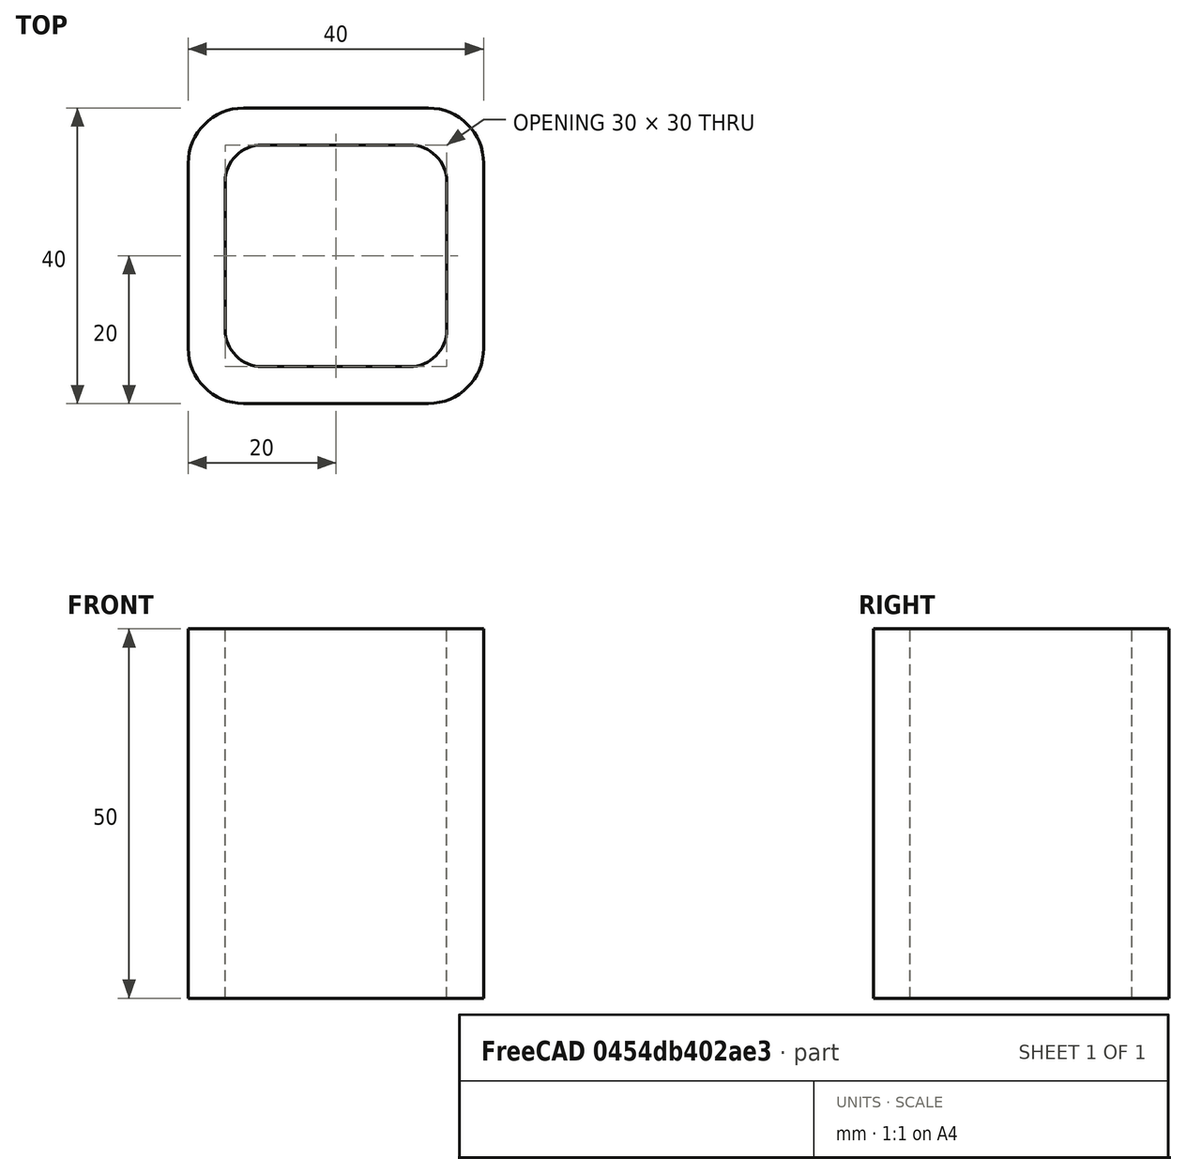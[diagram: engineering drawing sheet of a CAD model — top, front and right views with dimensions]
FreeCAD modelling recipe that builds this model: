
FCSTD DOCUMENT  (FreeCAD 0.15R4671 (Git))
Label: Square hollow section 40x40x5 EN10219 S235JRH
License: All rights reserved
LicenseURL: http://en.wikipedia.org/wiki/All_rights_reserved
objects: Sketcher::SketchObject×1, Part::Extrusion×1
note: 2 computed .brp shape members not serialized (recipe doc carries the construction recipe); baked Part::Feature solids carry a one-line shape summary decoded from their .brp

FEATURE [Sketcher::SketchObject] Sketch
  sketch-geometry (16):
    g0: LineSegment StartX=-10 StartY=15 StartZ=0 EndX=10 EndY=15 EndZ=0
    g1: LineSegment StartX=15 StartY=10 StartZ=0 EndX=15 EndY=-10 EndZ=0
    g2: LineSegment StartX=10 StartY=-15 StartZ=0 EndX=-10 EndY=-15 EndZ=0
    g3: LineSegment StartX=-15 StartY=-10 StartZ=0 EndX=-15 EndY=10 EndZ=0
    g4: LineSegment StartX=-12.5 StartY=20 StartZ=0 EndX=12.5 EndY=20 EndZ=0
    g5: LineSegment StartX=20 StartY=12.5 StartZ=0 EndX=20 EndY=-12.5 EndZ=0
    g6: LineSegment StartX=12.5 StartY=-20 StartZ=0 EndX=-12.5 EndY=-20 EndZ=0
    g7: LineSegment StartX=-20 StartY=-12.5 StartZ=0 EndX=-20 EndY=12.5 EndZ=0
    g8: ArcOfCircle CenterX=-10 CenterY=10 CenterZ=0 NormalX=0 NormalY=0 NormalZ=1 Radius=5 StartAngle=1.5708 EndAngle=3.14159
    g9: ArcOfCircle CenterX=10 CenterY=10 CenterZ=0 NormalX=0 NormalY=0 NormalZ=1 Radius=5 StartAngle=0 EndAngle=1.5708
    g10: ArcOfCircle CenterX=10 CenterY=-10 CenterZ=0 NormalX=0 NormalY=0 NormalZ=1 Radius=5 StartAngle=4.71239 EndAngle=6.28319
    g11: ArcOfCircle CenterX=-10 CenterY=-10 CenterZ=0 NormalX=0 NormalY=0 NormalZ=1 Radius=5 StartAngle=3.14159 EndAngle=4.71239
    g12: ArcOfCircle CenterX=12.5 CenterY=12.5 CenterZ=0 NormalX=0 NormalY=0 NormalZ=1 Radius=7.5 StartAngle=0 EndAngle=1.5708
    g13: ArcOfCircle CenterX=12.5 CenterY=-12.5 CenterZ=0 NormalX=0 NormalY=0 NormalZ=1 Radius=7.5 StartAngle=4.71239 EndAngle=6.28319
    g14: ArcOfCircle CenterX=-12.5 CenterY=-12.5 CenterZ=0 NormalX=0 NormalY=0 NormalZ=1 Radius=7.5 StartAngle=3.14159 EndAngle=4.71239
    g15: ArcOfCircle CenterX=-12.5 CenterY=12.5 CenterZ=0 NormalX=0 NormalY=0 NormalZ=1 Radius=7.5 StartAngle=1.5708 EndAngle=3.14159
  constraints (36):
    c: Horizontal(g2)
    c: Vertical(g3)
    c: Horizontal(g6)
    c: Vertical(g7)
    c: Tangent(g3,g8) = 1.5708
    c: Tangent(g0,g8) = 1.5708
    c: Tangent(g0,g9) = 1.5708
    c: Tangent(g1,g9) = 1.5708
    c: Tangent(g1,g10) = 1.5708
    c: Tangent(g2,g10) = 1.5708
    c: Tangent(g2,g11) = 1.5708
    c: Tangent(g3,g11) = 1.5708
    c: Tangent(g4,g12) = 1.5708
    c: Tangent(g5,g12) = 1.5708
    c: Tangent(g5,g13) = 1.5708
    c: Tangent(g6,g13) = 1.5708
    c: Tangent(g6,g14) = 1.5708
    c: Tangent(g7,g14) = 1.5708
    c: Tangent(g7,g15) = 1.5708
    c: Tangent(g4,g15) = 1.5708
    c: Equal(g9,g8)
    c: Equal(g9,g11)
    c: Equal(g9,g10)
    c: Equal(g12,g15)
    c: Equal(g12,g14)
    c: Equal(g12,g13)
    c: Symmetric(g4,g6,g-1)
    c: Symmetric(g7,g5,g-2)
    c: DistanceY(g4,g6) = -40
    c: DistanceX(g7,g5) = 40
    c: Symmetric(g3,g1,g-2)
    c: Symmetric(g0,g2,g-1)
    c: DistanceY(g0,g4) = 5
    c: DistanceX(g5,g1) = -5
    c: Radius(g9) = 5
    c: Radius(g12) = 7.5
FEATURE [Part::Extrusion] Extrude  label="Square hollow section 40x40x5 EN10219 S235JRH"
  Base = -> Sketch
  Dir = (0,0,50)
  Solid = true
